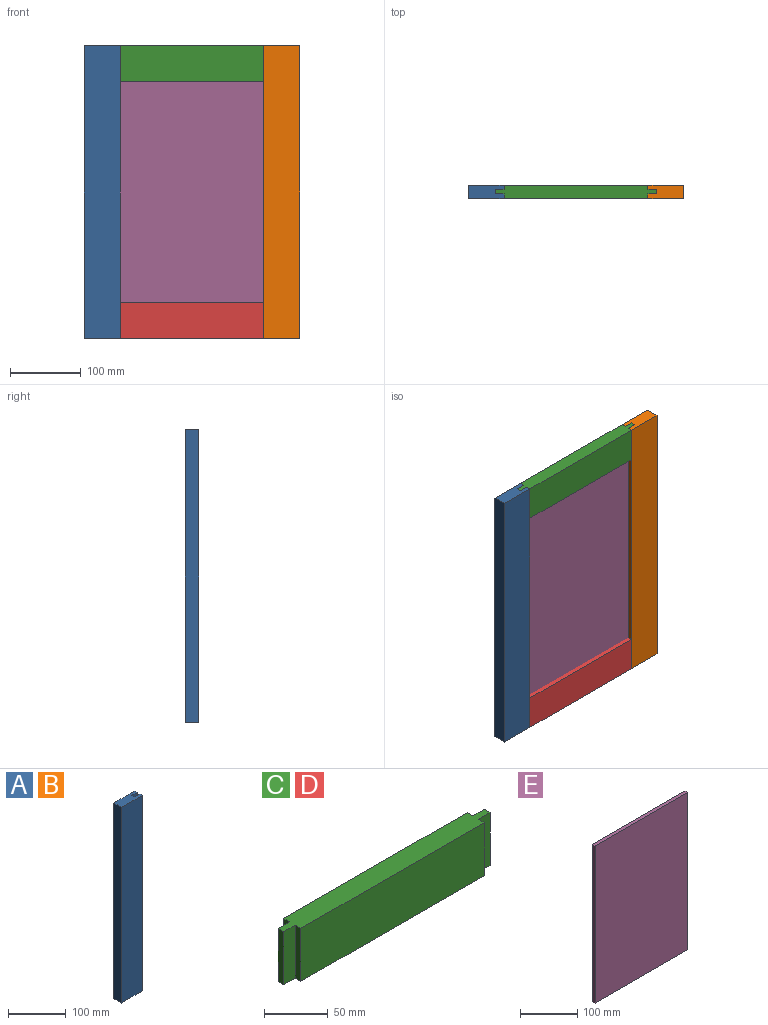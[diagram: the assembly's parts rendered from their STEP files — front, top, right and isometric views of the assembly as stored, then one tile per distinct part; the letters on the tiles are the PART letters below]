
ASSEMBLY  parts=5 mates=4
PART A: 10 faces, bbox 50.8x19.1x412.8 mm
  f0: plane 412.75x6.35mm, normal (1,0,0), area 2621mm2, adj f1,f3,f5,f7
  f1: plane 50.8x19.05mm, normal (0,0,-1), area 887.1mm2, adj f0,f2,f4,f5,f6,f7,f8,f9
  f2: plane 412.75x6.35mm, normal (1,0,0), area 2621mm2, adj f1,f3,f6,f9
  f3: plane 50.8x19.05mm, normal (0,0,1), area 887.1mm2, adj f0,f2,f4,f5,f6,f7,f8,f9
  f4: plane 412.75x19.05mm, normal (-1,0,0), area 7862.9mm2, adj f1,f3,f5,f6
  f5: plane 412.75x50.8mm, normal (0,-1,0), area 20967.7mm2, adj f0,f1,f3,f4
  f6: plane 412.75x50.8mm, normal (0,1,0), area 20967.7mm2, adj f1,f2,f3,f4
  f7: plane 412.75x12.7mm, normal (0,1,0), area 5241.9mm2, adj f0,f1,f3,f8
  f8: plane 412.75x6.35mm, normal (1,0,0), area 2621mm2, adj f1,f3,f7,f9
  f9: plane 412.75x12.7mm, normal (0,-1,0), area 5241.9mm2, adj f1,f2,f3,f8
PART B: same geometry as A
PART C: 14 faces, bbox 228.6x19.1x50.8 mm
  f0: plane 228.6x19.05mm, normal (0,0,-1), area 4032.3mm2, adj f1,f3,f4,f5,f6,f7,f8,f9
  f1: plane 50.8x6.35mm, normal (1,0,0), area 322.6mm2, adj f0,f2,f10,f12
  f2: plane 228.6x19.05mm, normal (0,0,1), area 4032.3mm2, adj f1,f3,f4,f5,f6,f7,f8,f9
  f3: plane 50.8x6.35mm, normal (-1,0,0), area 322.6mm2, adj f0,f2,f6,f8
  f4: plane 203.2x50.8mm, normal (0,-1,0), area 10322.6mm2, adj f0,f2,f9,f13
  f5: plane 203.2x50.8mm, normal (0,1,0), area 10322.6mm2, adj f0,f2,f7,f11
  f6: plane 50.8x12.7mm, normal (0,1,0), area 645.2mm2, adj f0,f2,f3,f7
  f7: plane 50.8x6.35mm, normal (-1,0,0), area 322.6mm2, adj f0,f2,f5,f6
  f8: plane 50.8x12.7mm, normal (0,-1,0), area 645.2mm2, adj f0,f2,f3,f9
  f9: plane 50.8x6.35mm, normal (-1,0,0), area 322.6mm2, adj f0,f2,f4,f8
  f10: plane 50.8x12.7mm, normal (0,1,0), area 645.2mm2, adj f0,f1,f2,f11
  f11: plane 50.8x6.35mm, normal (1,0,0), area 322.6mm2, adj f0,f2,f5,f10
  f12: plane 50.8x12.7mm, normal (0,-1,0), area 645.2mm2, adj f0,f1,f2,f13
  f13: plane 50.8x6.35mm, normal (1,0,0), area 322.6mm2, adj f0,f2,f4,f12
PART D: same geometry as C
PART E: 6 faces, bbox 228.6x6.4x336.6 mm
  f0: plane 336.55x6.35mm, normal (1,0,0), area 2137.1mm2, adj f1,f3,f4,f5
  f1: plane 228.6x6.35mm, normal (0,0,1), area 1451.6mm2, adj f0,f2,f4,f5
  f2: plane 336.55x6.35mm, normal (-1,0,0), area 2137.1mm2, adj f1,f3,f4,f5
  f3: plane 228.6x6.35mm, normal (0,0,-1), area 1451.6mm2, adj f0,f2,f4,f5
  f4: plane 336.55x228.6mm, normal (0,-1,0), area 76935.3mm2, adj f0,f1,f2,f3
  f5: plane 336.55x228.6mm, normal (0,1,0), area 76935.3mm2, adj f0,f1,f2,f3
PLACE A t=(-126.41,6.41,2.01)mm
PLACE B rot(axis=(0,-1,0),180deg) t=(127.59,6.41,2.01)mm
PLACE C t=(0.59,-3.12,182.98)mm
PLACE D t=(0.59,-3.12,-178.97)mm
PLACE E t=(0.59,-3.12,2.01)mm
MATE fastened E.f2 <-> A.f8  axis (-1,0,0) through (-113.71,-3.12,2.01)mm
MATE fastened C.f3 <-> A.f8  axis (-1,0,0) through (-113.71,-3.12,208.38)mm
MATE fastened D.f1 <-> B.f8  axis (1,0,0) through (114.89,-3.12,-204.37)mm
MATE fastened C.f1 <-> B.f8  axis (1,0,0) through (114.89,-3.12,208.38)mm
